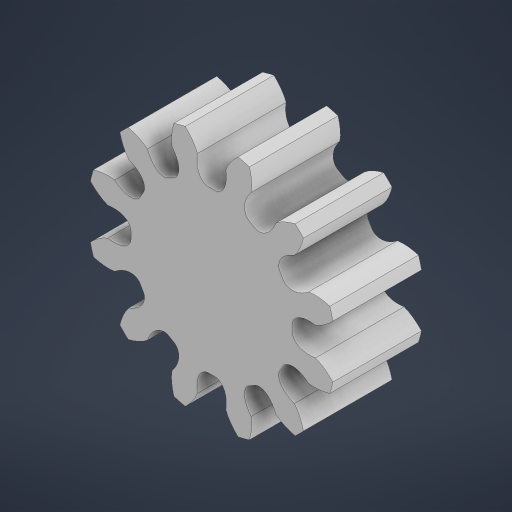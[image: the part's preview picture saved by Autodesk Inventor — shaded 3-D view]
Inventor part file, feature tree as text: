
AUTODESK INVENTOR PART (.ipt)
format: ipt  version: 2024.1 (Build 281209000, 209)  size: 322,048 bytes
history: native  units: in
note: dims shown in document units (in); Inventor stores cm internally (conversion verified against a paired STEP export)
features: extrude x2, pattern_circular x1
ambient origin geometry x8: Origin, YZ Plane, XZ Plane, XY Plane, X Axis, Y Axis, Z Axis, Center Point
bodies: Solid1 (feature_tree)
feature tree (3):
  extrude  "Extrusion1"  Depth=0.15in
  extrude  "Extrusion2"  TaperAngle=0.0deg  [1 undecoded]
  pattern_circular  "Circular Pattern1"  [2 undecoded]
note: 3 required parameter values undecoded (feature->parameter linkage not recoverable at this tier; creation-order binding heuristic only, values carry confidence <= 0.55)
